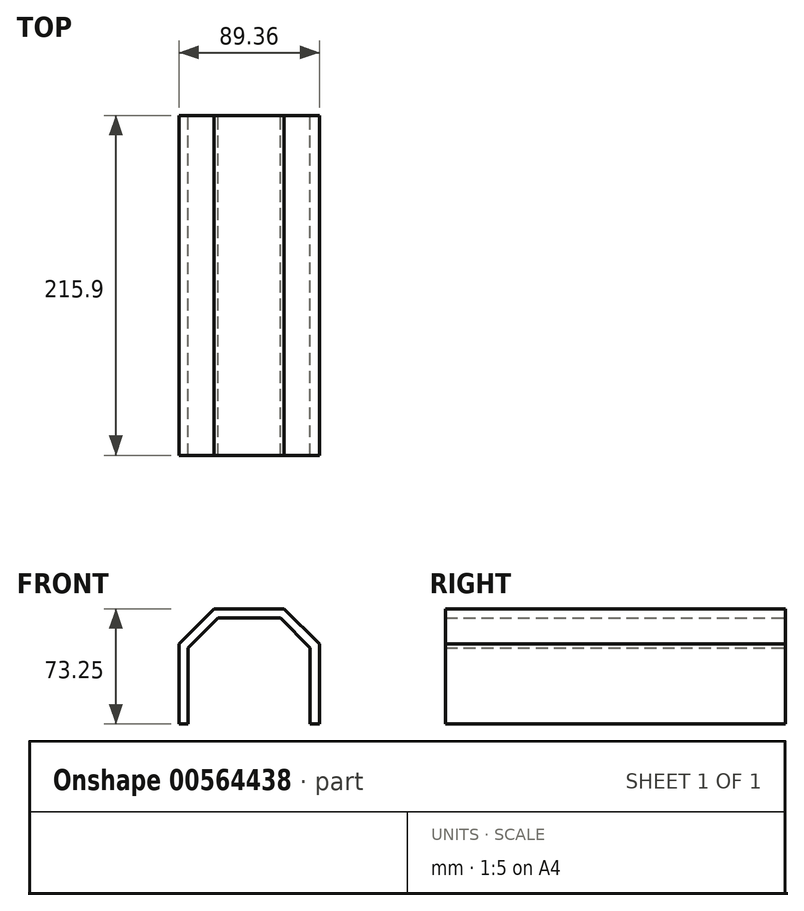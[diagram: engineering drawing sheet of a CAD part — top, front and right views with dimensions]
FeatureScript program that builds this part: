
annotation { "Feature Type Name" : "Feature", "Feature Type Description" : "" }
export const myFeature = defineFeature(function(context is Context, id is Id, definition is map)
    precondition{}
    {
        {
            var Q0;
            Q0=qCreatedBy(makeId("Front.planeOp"),FACE);
            var sketch = newSketch(context, id + "F0", { "sketchPlane" : qUnion([Q0])});
            skLineSegment(sketch, "E0.bottom", {"start": v(-44.68, 0) * mm, "end": v(-38.76, 0) * mm});
            skLineSegment(sketch, "E0.top", {"start": v(-44.68, 50.8) * mm, "end": v(-38.76, 48.35) * mm, "construction": true});
            skLineSegment(sketch, "E0.left", {"start": v(-44.68, 0) * mm, "end": v(-44.68, 50.8) * mm});
            skLineSegment(sketch, "E0.right", {"start": v(-38.76, 0) * mm, "end": v(-38.76, 48.35) * mm});
            skLineSegment(sketch, "E1", {"start": v(-44.68, 50.8) * mm, "end": v(-22.23, 73.25) * mm});
            skLineSegment(sketch, "E2", {"start": v(-22.22, 73.25) * mm, "end": v(-19.77, 67.33) * mm, "construction": true});
            skLineSegment(sketch, "E3", {"start": v(-19.77, 67.33) * mm, "end": v(-38.76, 48.35) * mm});
            skLineSegment(sketch, "E4", {"start": v(-22.23, 73.25) * mm, "end": v(0, 73.25) * mm});
            skLineSegment(sketch, "E5", {"start": v(0, 73.25) * mm, "end": v(0, 67.33) * mm, "construction": true});
            skLineSegment(sketch, "E6", {"start": v(0, 67.33) * mm, "end": v(-19.77, 67.33) * mm});
            skLineSegment(sketch, "E7.MirrorCS", {"start": v(22.23, 73.25) * mm, "end": v(0, 73.25) * mm});
            skLineSegment(sketch, "E8.MirrorCS", {"start": v(0, 67.33) * mm, "end": v(19.77, 67.33) * mm});
            skLineSegment(sketch, "E9.MirrorCS", {"start": v(44.68, 50.8) * mm, "end": v(22.23, 73.25) * mm});
            skLineSegment(sketch, "E10.MirrorCS", {"start": v(19.77, 67.33) * mm, "end": v(38.76, 48.35) * mm});
            skLineSegment(sketch, "E11.MirrorCS", {"start": v(38.76, 0) * mm, "end": v(38.76, 48.35) * mm});
            skLineSegment(sketch, "E12.MirrorCS", {"start": v(44.68, 0) * mm, "end": v(44.68, 50.8) * mm});
            skLineSegment(sketch, "E13.MirrorCS", {"start": v(44.68, 0) * mm, "end": v(38.76, 0) * mm});
            skSolve(sketch);
        }
        {
            var Q0;
            Q0=makeQuery(id+"F0.imprint","IMPRINT",FACE,{"disambiguationData":[TD([[makeQuery(id+"F0.imprint","IMPRINT",EDGE,{"derivedFrom":sQuery(id+"F0.wireOp",EDGE,"E0.bottom")}),1.0]])]});
            extrude(context, id + "F1", {"entities" : qUnion([Q0]), "flatOperationType" : FlatOperationType.REMOVE, "depth" : 215.9 * mm, "offsetDistance" : 25.4 * mm, "domain" : OperationDomain.MODEL, "symmetric" : true});
        }
    });
